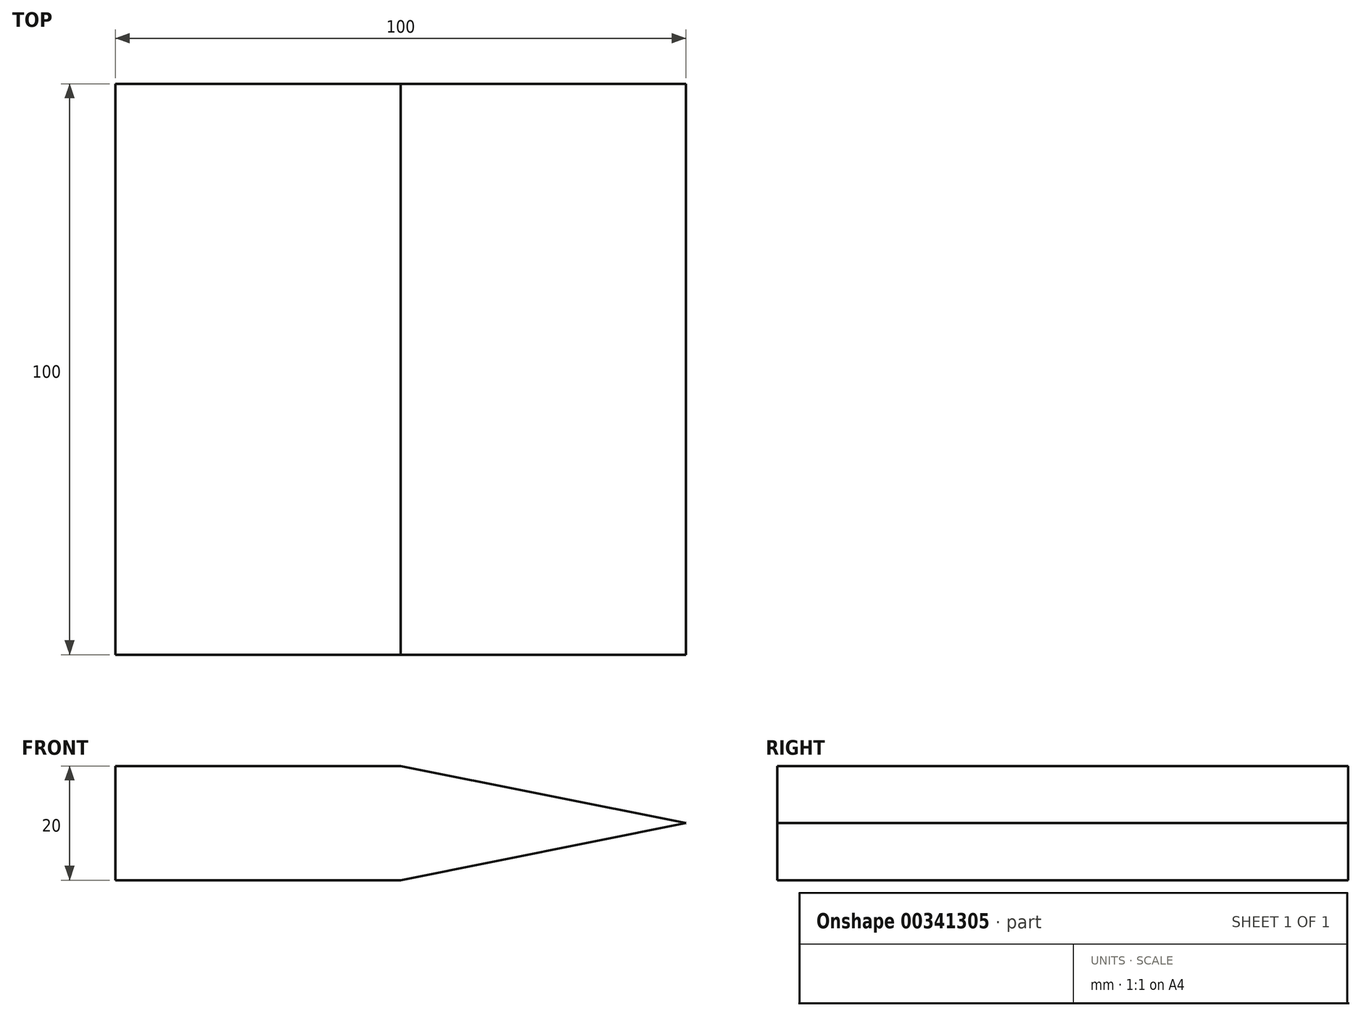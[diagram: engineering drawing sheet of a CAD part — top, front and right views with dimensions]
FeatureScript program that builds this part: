
annotation { "Feature Type Name" : "Feature", "Feature Type Description" : "" }
export const myFeature = defineFeature(function(context is Context, id is Id, definition is map)
    precondition{}
    {
        {
            var Q0;
            Q0=qCreatedBy(makeId("Front.planeOp"),FACE);
            var sketch = newSketch(context, id + "F0", { "sketchPlane" : qUnion([Q0])});
            skLineSegment(sketch, "E0.bottom", {"start": v(0, 0) * mm, "end": v(50, 0) * mm});
            skLineSegment(sketch, "E0.top", {"start": v(0, 20) * mm, "end": v(50, 20) * mm});
            skLineSegment(sketch, "E0.left", {"start": v(0, 0) * mm, "end": v(0, 20) * mm});
            skLineSegment(sketch, "E0.right", {"start": v(50, 0) * mm, "end": v(50, 20) * mm});
            skLineSegment(sketch, "E1", {"start": v(50, 10) * mm, "end": v(100, 10) * mm});
            skLineSegment(sketch, "E2", {"start": v(100, 10) * mm, "end": v(50, 20) * mm});
            skLineSegment(sketch, "E3", {"start": v(100, 10) * mm, "end": v(50, 0) * mm});
            skSolve(sketch);
        }
        {
            var Q0;
            {var subQ1=sQuery(id+"F0.wireOp",EDGE,"E0.bottom");Q0=makeQuery(id+"F0.imprint","IMPRINT",FACE,{"disambiguationData":[TD([[makeQuery(id+"F0.imprint","IMPRINT",EDGE,{"derivedFrom":subQ1}),1.0]])]});}
            var Q1;
            {var subQ2=sQuery(id+"F0.wireOp",EDGE,"E1");Q1=makeQuery(id+"F0.imprint","IMPRINT",FACE,{"disambiguationData":[TD([[makeQuery(id+"F0.imprint","IMPRINT",EDGE,{"derivedFrom":subQ2}),1.0]])]});}
            var Q2;
            {var subQ2=sQuery(id+"F0.wireOp",EDGE,"E1");Q2=makeQuery(id+"F0.imprint","IMPRINT",FACE,{"disambiguationData":[TD([[makeQuery(id+"F0.imprint","IMPRINT",EDGE,{"derivedFrom":subQ2}),-1.0]])]});}
            extrude(context, id + "F1", {"entities" : qUnion([Q0, Q1, Q2]), "depth" : 100 * mm});
        }
    });
